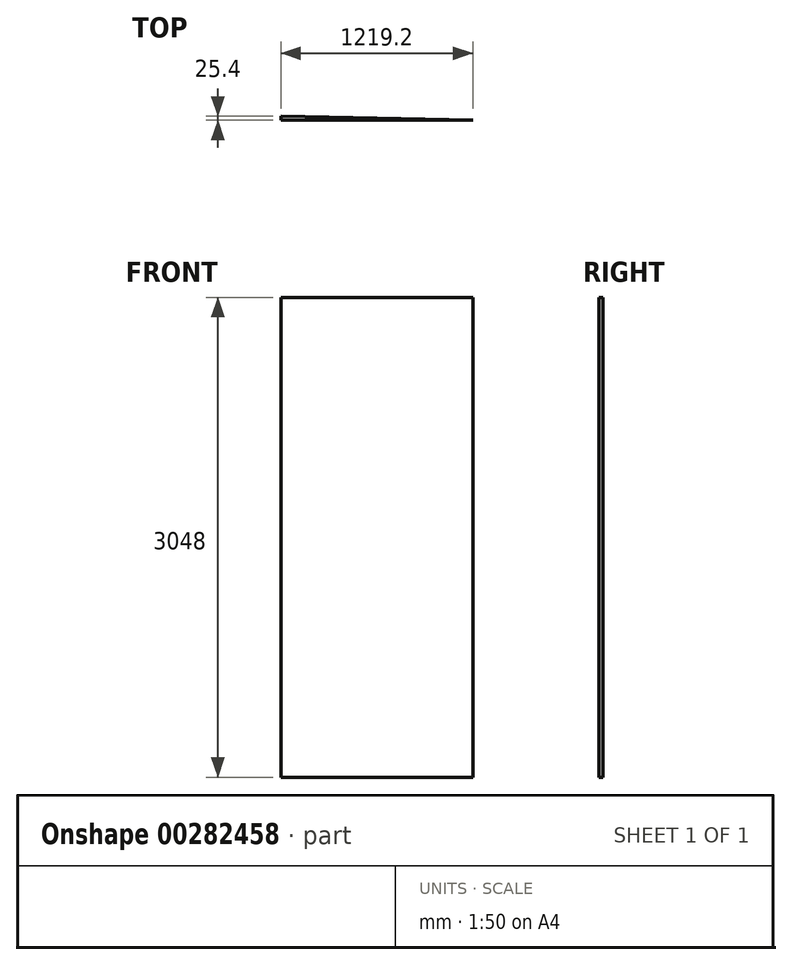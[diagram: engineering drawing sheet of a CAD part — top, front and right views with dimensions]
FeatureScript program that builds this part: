
annotation { "Feature Type Name" : "Feature", "Feature Type Description" : "" }
export const myFeature = defineFeature(function(context is Context, id is Id, definition is map)
    precondition{}
    {
        {
            var Q0;
            Q0=qCreatedBy(makeId("Front.planeOp"),FACE);
            var sketch = newSketch(context, id + "F2", { "sketchPlane" : qUnion([Q0])});
            skLineSegment(sketch, "E0.bottom", {"start": v(609.6, -1524) * mm, "end": v(-609.6, -1524) * mm});
            skLineSegment(sketch, "E0.top", {"start": v(609.6, 1524) * mm, "end": v(-609.6, 1524) * mm});
            skLineSegment(sketch, "E0.left", {"start": v(609.6, -1524) * mm, "end": v(609.6, 1524) * mm});
            skLineSegment(sketch, "E0.right", {"start": v(-609.6, -1524) * mm, "end": v(-609.6, 1524) * mm});
            skPoint(sketch, "E0.middle", {"position": v(0, 0) * mm});
            skSolve(sketch);
        }
        {
            var Q0;
            Q0=makeQuery(id+"F2.imprint","IMPRINT",FACE,{"disambiguationData":[TD([[makeQuery(id+"F2.imprint","IMPRINT",EDGE,{"derivedFrom":sQuery(id+"F2.wireOp",EDGE,"E0.bottom")}),-1.0]])]});
            extrude(context, id + "F0", {"entities" : qUnion([Q0]), "depth" : 25.4 * mm});
        }
        {
            var Q0;
            Q0=makeQuery(id+"F0.opExtrude","SWEPT_FACE",FACE,{"disambiguationData":[OSD([sQuery(id+"F2.wireOp",EDGE,"E0.bottom")])]});
            var sketch = newSketch(context, id + "F1", { "sketchPlane" : qUnion([Q0])});
            skLineSegment(sketch, "E1", {"start": v(609.6, 25.4) * mm, "end": v(-609.6, 0) * mm});
            skSolve(sketch);
        }
        {
            var Q0;
            Q0=makeQuery(id+"F1.imprint","IMPRINT",FACE,{"disambiguationData":[TD([[makeQuery(id+"F1.imprint","IMPRINT",EDGE,{"derivedFrom":sQuery(id+"F1.wireOp",EDGE,"E1")}),1.0]])]});
            extrude(context, id + "F3", {"entities" : qUnion([Q0]), "operationType" : NewBodyOperationType.REMOVE, "oppositeDirection" : true, "depth" : 3048 * mm});
        }
    });
